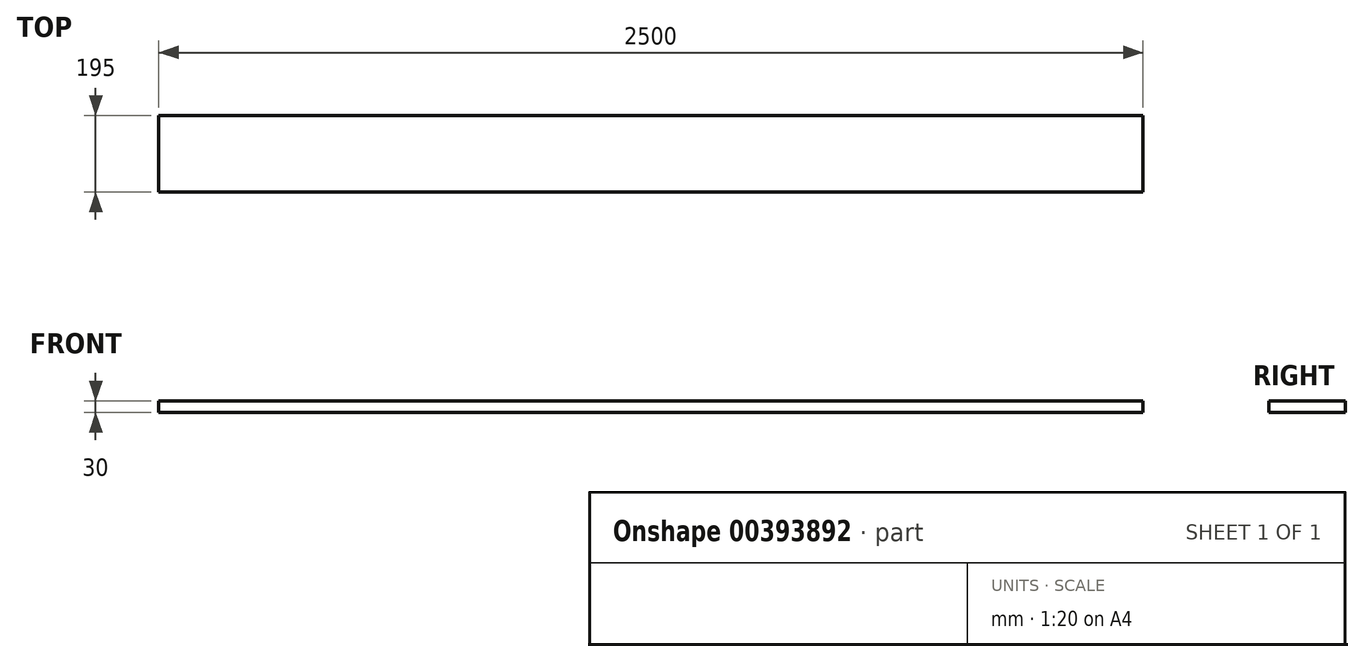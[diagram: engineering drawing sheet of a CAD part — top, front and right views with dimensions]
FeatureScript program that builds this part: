
annotation { "Feature Type Name" : "Feature", "Feature Type Description" : "" }
export const myFeature = defineFeature(function(context is Context, id is Id, definition is map)
    precondition{}
    {
        {
            var Q0;
            Q0=qCreatedBy(makeId("Top.planeOp"),FACE);
            var sketch = newSketch(context, id + "F0", { "sketchPlane" : qUnion([Q0])});
            skLineSegment(sketch, "E0.bottom", {"start": v(1250, 97.5) * mm, "end": v(-1250, 97.5) * mm});
            skLineSegment(sketch, "E0.top", {"start": v(1250, -97.5) * mm, "end": v(-1250, -97.5) * mm});
            skLineSegment(sketch, "E0.left", {"start": v(1250, 97.5) * mm, "end": v(1250, -97.5) * mm});
            skLineSegment(sketch, "E0.right", {"start": v(-1250, 97.5) * mm, "end": v(-1250, -97.5) * mm});
            skPoint(sketch, "E0.middle", {"position": v(0, 0) * mm});
            skSolve(sketch);
        }
        {
            var Q0;
            Q0=makeQuery(id+"F0.imprint","IMPRINT",FACE,{"disambiguationData":[TD([[makeQuery(id+"F0.imprint","IMPRINT",EDGE,{"derivedFrom":sQuery(id+"F0.wireOp",EDGE,"E0.bottom")}),1.0]])]});
            extrude(context, id + "F1", {"entities" : qUnion([Q0]), "endBound" : BoundingType.SYMMETRIC, "depth" : 30 * mm});
        }
    });
